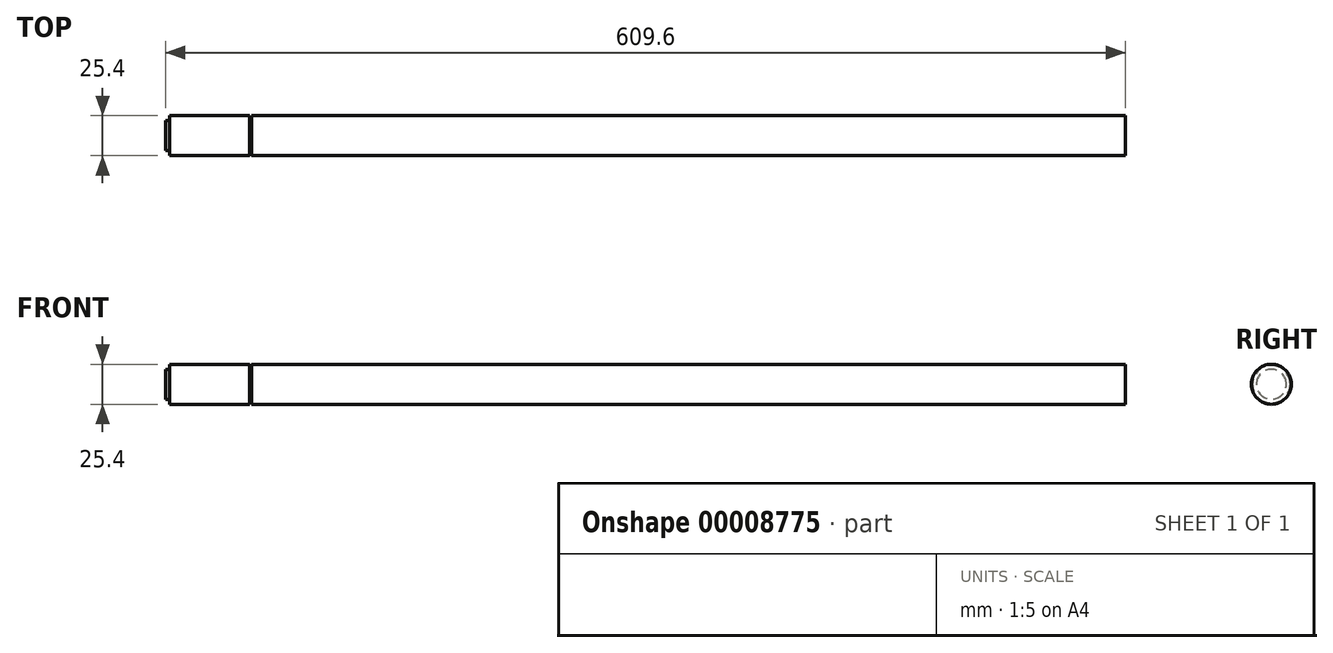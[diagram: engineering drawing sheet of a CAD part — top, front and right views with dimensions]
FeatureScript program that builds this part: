
annotation { "Feature Type Name" : "Feature", "Feature Type Description" : "" }
export const myFeature = defineFeature(function(context is Context, id is Id, definition is map)
    precondition{}
    {
        {
            var Q0;
            Q0=qCreatedBy(makeId("Front.planeOp"),FACE);
            var sketch = newSketch(context, id + "F0", { "sketchPlane" : qUnion([Q0])});
            skLineSegment(sketch, "E0.rect.bottom", {"start": v(304.8, 12.7) * mm, "end": v(-250.3, 12.7) * mm});
            skLineSegment(sketch, "E0.rect.left", {"start": v(304.8, 12.7) * mm, "end": v(304.8, 0) * mm});
            skLineSegment(sketch, "E0.rect.right", {"start": v(-304.8, 9.52) * mm, "end": v(-304.8, 0) * mm});
            skPoint(sketch, "E0.rect.middle", {"position": v(0, 0) * mm});
            skLineSegment(sketch, "E1", {"start": v(-302.26, 12.7) * mm, "end": v(-302.26, 9.52) * mm});
            skLineSegment(sketch, "E2", {"start": v(-304.8, 0) * mm, "end": v(304.8, 0) * mm});
            skLineSegment(sketch, "E3", {"start": v(-304.8, 9.52) * mm, "end": v(-302.26, 9.52) * mm});
            skLineSegment(sketch, "E4", {"start": v(-251.46, 12.7) * mm, "end": v(-251.46, 11.94) * mm});
            skLineSegment(sketch, "E5", {"start": v(-251.46, 11.94) * mm, "end": v(-250.3, 11.94) * mm});
            skLineSegment(sketch, "E6", {"start": v(-250.3, 11.94) * mm, "end": v(-250.3, 12.7) * mm});
            skLineSegment(sketch, "E7.trimOffspring", {"start": v(-251.46, 12.7) * mm, "end": v(-302.26, 12.7) * mm});
            skSolve(sketch);
        }
        {
            var Q0;
            Q0=makeQuery(id+"F0.imprint","IMPRINT",FACE,{"disambiguationData":[TD([[makeQuery(id+"F0.imprint","IMPRINT",EDGE,{"derivedFrom":sQuery(id+"F0.wireOp",EDGE,"E0.rect.bottom")}),1.0]])]});
            var Q1;
            Q1=sQuery(id+"F0.wireOp",EDGE,"E2");
            revolve(context, id + "F1", {"entities" : qUnion([Q0]), "axis" : qUnion([Q1]), "revolveType" : RevolveType.FULL});
        }
    });
